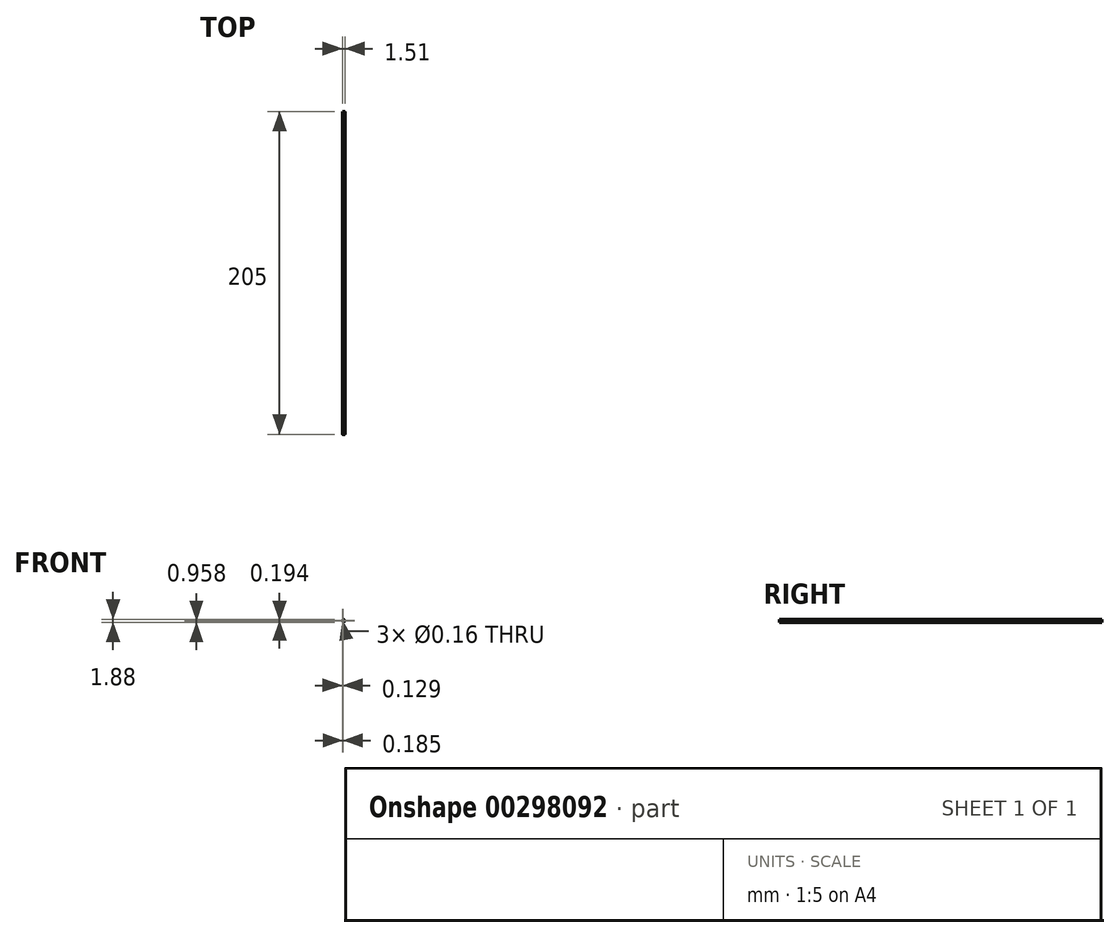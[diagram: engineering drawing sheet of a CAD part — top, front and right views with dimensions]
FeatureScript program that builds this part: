
annotation { "Feature Type Name" : "Feature", "Feature Type Description" : "" }
export const myFeature = defineFeature(function(context is Context, id is Id, definition is map)
    precondition{}
    {
        {
            var Q0;
            Q0=qCreatedBy(makeId("Front.planeOp"),FACE);
            var sketch = newSketch(context, id + "F0", { "sketchPlane" : qUnion([Q0])});
            skCircle(sketch, "E0", {"center": v(0, 0) * mm, "radius": 0.4 * mm});
            skCircle(sketch, "E1", {"center": v(-0.1, -0.56) * mm, "radius": 0.08 * mm});
            skCircle(sketch, "E2", {"center": v(0.1, -0.56) * mm, "radius": 0.08 * mm});
            skCircle(sketch, "E3", {"center": v(0, 0.84) * mm, "radius": 0.4 * mm});
            skCircle(sketch, "E4", {"center": v(0.65, 0.51) * mm, "radius": 0.08 * mm});
            skCircle(sketch, "E5", {"center": v(0.65, 0.32) * mm, "radius": 0.08 * mm});
            skCircle(sketch, "E6", {"center": v(0.47, 0.42) * mm, "radius": 0.08 * mm});
            skCircle(sketch, "E7", {"center": v(0.56, 0.42) * mm, "radius": 0.22 * mm});
            skEllipse(sketch, "E8", {"center": v(0, -0.56) * mm, "majorRadius": 0.23 * mm, "minorRadius": 0.11 * mm, "majorAxis": v(1, 0)});
            skCircle(sketch, "E9.MirrorC", {"center": v(-0.56, 0.42) * mm, "radius": 0.22 * mm});
            skCircle(sketch, "E10.MirrorC", {"center": v(-0.65, 0.51) * mm, "radius": 0.08 * mm});
            skCircle(sketch, "E11.MirrorC", {"center": v(-0.47, 0.42) * mm, "radius": 0.08 * mm});
            skCircle(sketch, "E12.MirrorC", {"center": v(-0.65, 0.32) * mm, "radius": 0.08 * mm});
            skPoint(sketch, "E13", {"position": v(0, 1.24) * mm});
            skPoint(sketch, "E14", {"position": v(0, -0.67) * mm});
            skPoint(sketch, "E15", {"position": v(0, 0.29) * mm});
            skCircle(sketch, "E16", {"center": v(0, 0.29) * mm, "radius": 1.2 * mm});
            skCircle(sketch, "E17", {"center": v(0, 0.29) * mm, "radius": 1.05 * mm});
            skSolve(sketch);
        }
        {
            var Q0;
            Q0=makeQuery(id+"F0.imprint","IMPRINT",FACE,{"disambiguationData":[TD([[makeQuery(id+"F0.imprint","IMPRINT",EDGE,{"derivedFrom":sQuery(id+"F0.wireOp",EDGE,"E3")}),1.0]])]});
            var Q1;
            Q1=makeQuery(id+"F0.imprint","IMPRINT",FACE,{"disambiguationData":[TD([[makeQuery(id+"F0.imprint","IMPRINT",EDGE,{"derivedFrom":sQuery(id+"F0.wireOp",EDGE,"E0")}),1.0]])]});
            var Q2;
            Q2=makeQuery(id+"F0.imprint","IMPRINT",FACE,{"disambiguationData":[TD([[makeQuery(id+"F0.imprint","IMPRINT",EDGE,{"derivedFrom":sQuery(id+"F0.wireOp",EDGE,"E11.MirrorC")}),-1.0]])]});
            var Q3;
            Q3=makeQuery(id+"F0.imprint","IMPRINT",FACE,{"disambiguationData":[TD([[makeQuery(id+"F0.imprint","IMPRINT",EDGE,{"derivedFrom":sQuery(id+"F0.wireOp",EDGE,"E10.MirrorC")}),-1.0]])]});
            var Q4;
            Q4=makeQuery(id+"F0.imprint","IMPRINT",FACE,{"disambiguationData":[TD([[makeQuery(id+"F0.imprint","IMPRINT",EDGE,{"derivedFrom":sQuery(id+"F0.wireOp",EDGE,"E12.MirrorC")}),-1.0]])]});
            var Q5;
            Q5=makeQuery(id+"F0.imprint","IMPRINT",FACE,{"disambiguationData":[TD([[makeQuery(id+"F0.imprint","IMPRINT",EDGE,{"derivedFrom":sQuery(id+"F0.wireOp",EDGE,"E6")}),1.0]])]});
            var Q6;
            Q6=makeQuery(id+"F0.imprint","IMPRINT",FACE,{"disambiguationData":[TD([[makeQuery(id+"F0.imprint","IMPRINT",EDGE,{"derivedFrom":sQuery(id+"F0.wireOp",EDGE,"E4")}),1.0]])]});
            var Q7;
            Q7=makeQuery(id+"F0.imprint","IMPRINT",FACE,{"disambiguationData":[TD([[makeQuery(id+"F0.imprint","IMPRINT",EDGE,{"derivedFrom":sQuery(id+"F0.wireOp",EDGE,"E5")}),1.0]])]});
            var Q8;
            Q8=makeQuery(id+"F0.imprint","IMPRINT",FACE,{"disambiguationData":[TD([[makeQuery(id+"F0.imprint","IMPRINT",EDGE,{"derivedFrom":sQuery(id+"F0.wireOp",EDGE,"E2")}),1.0]])]});
            var Q9;
            Q9=makeQuery(id+"F0.imprint","IMPRINT",FACE,{"disambiguationData":[TD([[makeQuery(id+"F0.imprint","IMPRINT",EDGE,{"derivedFrom":sQuery(id+"F0.wireOp",EDGE,"E1")}),1.0]])]});
            extrude(context, id + "F1", {"entities" : qUnion([Q0, Q1, Q2, Q3, Q4, Q5, Q6, Q7, Q8, Q9]), "depth" : 205 * mm});
        }
    });
